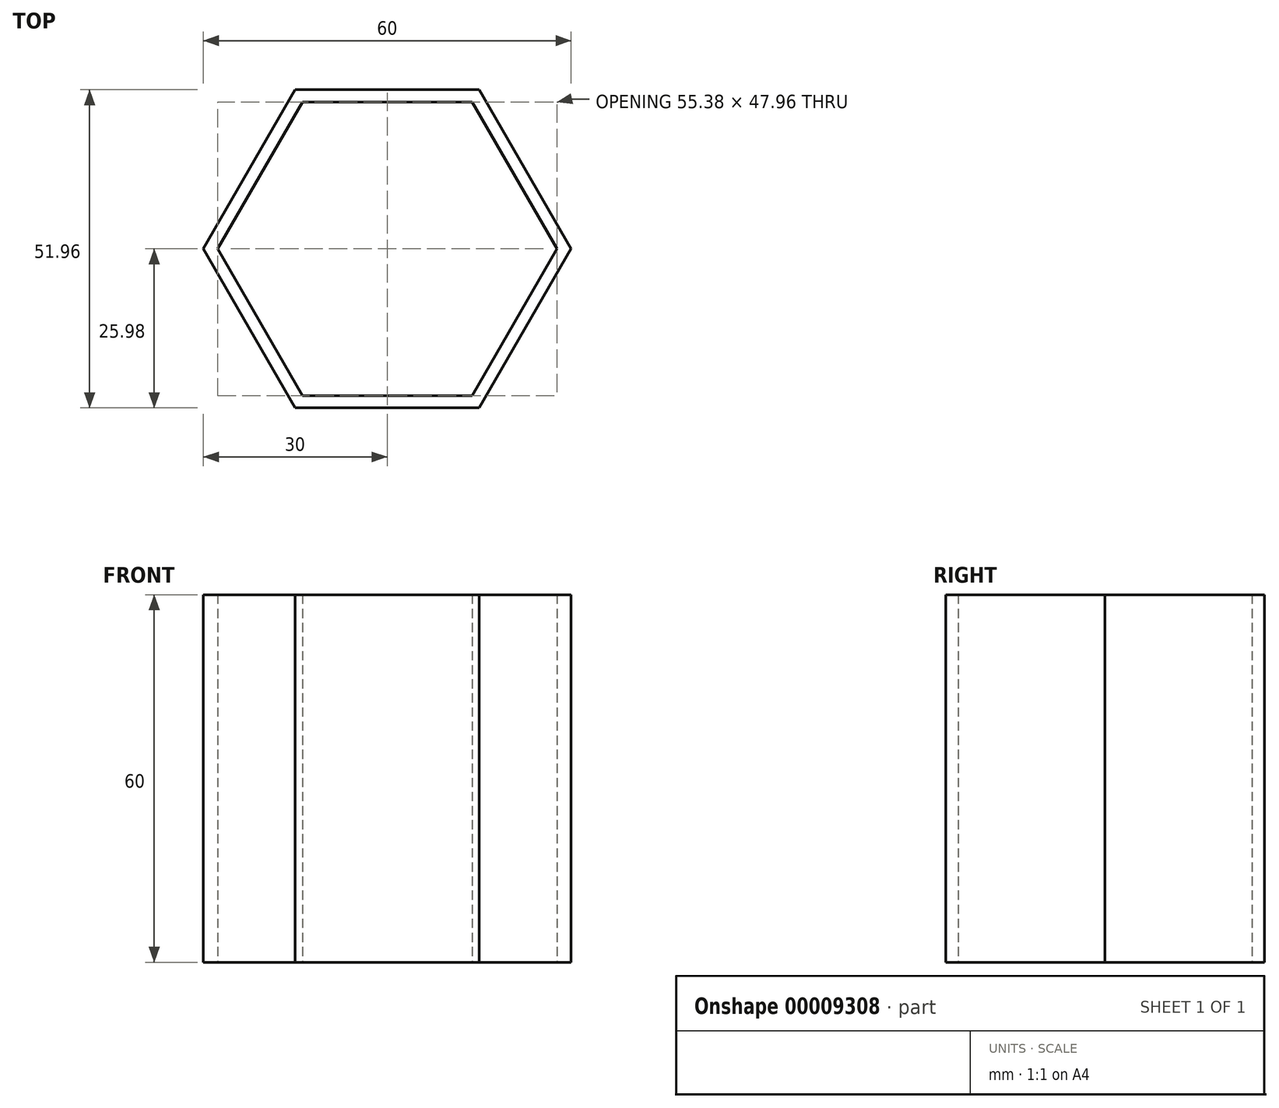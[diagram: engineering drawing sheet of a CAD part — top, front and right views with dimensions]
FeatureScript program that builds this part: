
annotation { "Feature Type Name" : "Feature", "Feature Type Description" : "" }
export const myFeature = defineFeature(function(context is Context, id is Id, definition is map)
    precondition{}
    {
        {
            var Q0;
            Q0=qCreatedBy(makeId("Top.planeOp"),FACE);
            var sketch = newSketch(context, id + "F0", { "sketchPlane" : qUnion([Q0])});
            skCircle(sketch, "E0.cCircle", {"center": v(0, 0) * mm, "radius": 30 * mm, "construction": true});
            skLineSegment(sketch, "E0.0", {"start": v(30, 0) * mm, "end": v(15, -25.98) * mm});
            skLineSegment(sketch, "E0.1", {"start": v(15, -25.98) * mm, "end": v(-15, -25.98) * mm});
            skLineSegment(sketch, "E0.2", {"start": v(-15, -25.98) * mm, "end": v(-30, 0) * mm});
            skLineSegment(sketch, "E0.3", {"start": v(-30, 0) * mm, "end": v(-15, 25.98) * mm});
            skLineSegment(sketch, "E0.4", {"start": v(-15, 25.98) * mm, "end": v(15, 25.98) * mm});
            skLineSegment(sketch, "E0.5", {"start": v(15, 25.98) * mm, "end": v(30, 0) * mm});
            skLineSegment(sketch, "E1.0", {"start": v(-13.85, 23.98) * mm, "end": v(13.85, 23.98) * mm});
            skLineSegment(sketch, "E1.1", {"start": v(-27.7, 0) * mm, "end": v(-13.85, 23.98) * mm});
            skLineSegment(sketch, "E1.2", {"start": v(-13.85, -23.98) * mm, "end": v(-27.7, 0) * mm});
            skLineSegment(sketch, "E1.3", {"start": v(13.85, -23.98) * mm, "end": v(-13.85, -23.98) * mm});
            skLineSegment(sketch, "E1.4", {"start": v(27.7, 0) * mm, "end": v(13.85, -23.98) * mm});
            skLineSegment(sketch, "E1.5", {"start": v(13.85, 23.98) * mm, "end": v(27.7, 0) * mm});
            skSolve(sketch);
        }
        {
            var Q0;
            Q0 = qSketchRegion(id + "F0", true);
            extrude(context, id + "F1", {"entities" : qUnion([Q0]), "depth" : 60 * mm});
        }
    });
